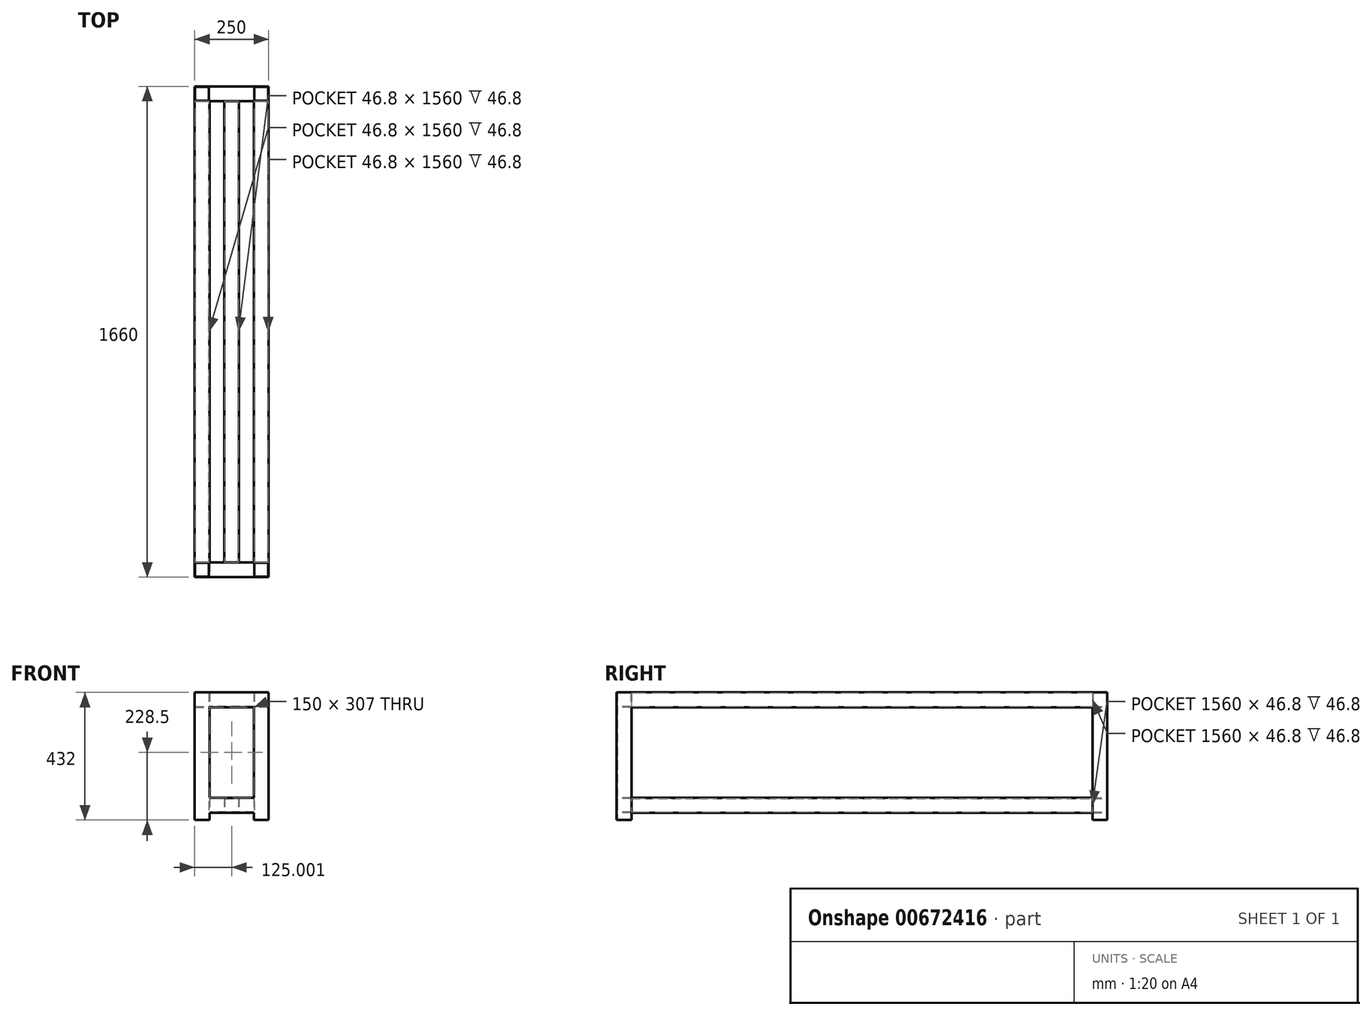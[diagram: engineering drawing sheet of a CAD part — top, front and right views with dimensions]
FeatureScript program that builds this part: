
annotation { "Feature Type Name" : "Feature", "Feature Type Description" : "" }
export const myFeature = defineFeature(function(context is Context, id is Id, definition is map)
    precondition{}
    {
        {
            var Q0;
            Q0=qCreatedBy(makeId("Top.planeOp"),FACE);
            var sketch = newSketch(context, id + "F0", { "sketchPlane" : qUnion([Q0])});
            skLineSegment(sketch, "E0.bottom", {"start": v(-25.56, 22.59) * mm, "end": v(24.44, 22.59) * mm});
            skLineSegment(sketch, "E0.top", {"start": v(-25.56, -27.41) * mm, "end": v(24.44, -27.41) * mm});
            skLineSegment(sketch, "E0.left", {"start": v(-25.56, 22.59) * mm, "end": v(-25.56, -27.41) * mm});
            skLineSegment(sketch, "E0.right", {"start": v(24.44, 22.59) * mm, "end": v(24.44, -27.41) * mm});
            skLineSegment(sketch, "E1.bottom", {"start": v(-23.96, 20.99) * mm, "end": v(22.84, 20.99) * mm});
            skLineSegment(sketch, "E1.top", {"start": v(-23.96, -25.81) * mm, "end": v(22.84, -25.81) * mm});
            skLineSegment(sketch, "E1.left", {"start": v(-23.96, 20.99) * mm, "end": v(-23.96, -25.81) * mm});
            skLineSegment(sketch, "E1.right", {"start": v(22.84, 20.99) * mm, "end": v(22.84, -25.81) * mm});
            skSolve(sketch);
        }
        {
            var Q0;
            Q0 = qSketchRegion(id + "F0", true);
            extrude(context, id + "F1", {"entities" : qUnion([Q0]), "depth" : 432 * mm, "offsetDistance" : 25 * mm});
        }
        {
            var Q0;
            Q0=makeQuery(id+"F1.opExtrude","SWEPT_FACE",FACE,{"disambiguationData":[OSD([sQuery(id+"F0.wireOp",EDGE,"E0.right")])]});
            var sketch = newSketch(context, id + "F2", { "sketchPlane" : qUnion([Q0])});
            skLineSegment(sketch, "E2.bottom", {"start": v(-27.41, 75) * mm, "end": v(22.59, 75) * mm});
            skLineSegment(sketch, "E2.top", {"start": v(-27.41, 25) * mm, "end": v(22.59, 25) * mm});
            skLineSegment(sketch, "E2.left", {"start": v(-27.41, 75) * mm, "end": v(-27.41, 25) * mm});
            skLineSegment(sketch, "E2.right", {"start": v(22.59, 75) * mm, "end": v(22.59, 25) * mm});
            skLineSegment(sketch, "E3.bottom", {"start": v(-25.81, 73.4) * mm, "end": v(20.99, 73.4) * mm});
            skLineSegment(sketch, "E3.top", {"start": v(-25.81, 26.6) * mm, "end": v(20.99, 26.6) * mm});
            skLineSegment(sketch, "E3.left", {"start": v(-25.81, 73.4) * mm, "end": v(-25.81, 26.6) * mm});
            skLineSegment(sketch, "E3.right", {"start": v(20.99, 73.4) * mm, "end": v(20.99, 26.6) * mm});
            skLineSegment(sketch, "E4.bottom", {"start": v(-27.41, 432) * mm, "end": v(22.59, 432) * mm});
            skLineSegment(sketch, "E4.top", {"start": v(-27.41, 382) * mm, "end": v(22.59, 382) * mm});
            skLineSegment(sketch, "E4.left", {"start": v(-27.41, 432) * mm, "end": v(-27.41, 382) * mm});
            skLineSegment(sketch, "E4.right", {"start": v(22.59, 432) * mm, "end": v(22.59, 382) * mm});
            skLineSegment(sketch, "E5.bottom", {"start": v(-25.81, 430.4) * mm, "end": v(20.99, 430.4) * mm});
            skLineSegment(sketch, "E5.top", {"start": v(-25.81, 383.6) * mm, "end": v(20.99, 383.6) * mm});
            skLineSegment(sketch, "E5.left", {"start": v(-25.81, 430.4) * mm, "end": v(-25.81, 383.6) * mm});
            skLineSegment(sketch, "E5.right", {"start": v(20.99, 430.4) * mm, "end": v(20.99, 383.6) * mm});
            skSolve(sketch);
        }
        {
            var Q0;
            Q0 = qSketchRegion(id + "F2", true);
            extrude(context, id + "F3", {"entities" : qUnion([Q0]), "operationType" : NewBodyOperationType.ADD, "depth" : 75 * mm, "offsetDistance" : 25 * mm});
        }
        {
            var Q0;
            Q0=makeQuery(id+"F3.boolean.opBoolean","MERGE",FACE,{"derivedFrom":[makeQuery(id+"F1.opExtrude","SWEPT_FACE",FACE,{"disambiguationData":[OSD([sQuery(id+"F0.wireOp",EDGE,"E0.top")])]}),makeQuery(id+"F3.opExtrude","SWEPT_FACE",FACE,{"disambiguationData":[OSD([sQuery(id+"F2.wireOp",EDGE,"E2.left")])]}),makeQuery(id+"F3.opExtrude","SWEPT_FACE",FACE,{"disambiguationData":[OSD([sQuery(id+"F2.wireOp",EDGE,"E4.left")])]})]});
            var sketch = newSketch(context, id + "F4", { "sketchPlane" : qUnion([Q0])});
            skLineSegment(sketch, "E6.bottom", {"start": v(-25.56, 432) * mm, "end": v(24.44, 432) * mm});
            skLineSegment(sketch, "E6.top", {"start": v(-25.56, 382) * mm, "end": v(24.44, 382) * mm});
            skLineSegment(sketch, "E6.left", {"start": v(-25.56, 432) * mm, "end": v(-25.56, 382) * mm});
            skLineSegment(sketch, "E6.right", {"start": v(24.44, 432) * mm, "end": v(24.44, 382) * mm});
            skLineSegment(sketch, "E7.bottom", {"start": v(-23.96, 430.4) * mm, "end": v(22.84, 430.4) * mm});
            skLineSegment(sketch, "E7.top", {"start": v(-23.96, 383.6) * mm, "end": v(22.84, 383.6) * mm});
            skLineSegment(sketch, "E7.left", {"start": v(-23.96, 430.4) * mm, "end": v(-23.96, 383.6) * mm});
            skLineSegment(sketch, "E7.right", {"start": v(22.84, 430.4) * mm, "end": v(22.84, 383.6) * mm});
            skLineSegment(sketch, "E8.bottom", {"start": v(74.44, 75) * mm, "end": v(99.44, 75) * mm});
            skLineSegment(sketch, "E8.top", {"start": v(74.44, 25) * mm, "end": v(99.44, 25) * mm});
            skLineSegment(sketch, "E8.left", {"start": v(74.44, 75) * mm, "end": v(74.44, 25) * mm});
            skLineSegment(sketch, "E8.right", {"start": v(99.44, 75) * mm, "end": v(99.44, 73.4) * mm});
            skLineSegment(sketch, "E9.bottom", {"start": v(76.04, 73.4) * mm, "end": v(99.44, 73.4) * mm});
            skLineSegment(sketch, "E9.top", {"start": v(76.04, 26.6) * mm, "end": v(99.44, 26.6) * mm});
            skLineSegment(sketch, "E9.left", {"start": v(76.04, 73.4) * mm, "end": v(76.04, 26.6) * mm});
            skLineSegment(sketch, "E10.trimOffspring", {"start": v(99.44, 26.6) * mm, "end": v(99.44, 25) * mm});
            skSolve(sketch);
        }
        {
            var Q0;
            Q0 = qSketchRegion(id + "F4", true);
            extrude(context, id + "F5", {"entities" : qUnion([Q0]), "operationType" : NewBodyOperationType.ADD, "depth" : 780 * mm, "offsetDistance" : 25 * mm});
        }
        {
            var Q0;
            Q0=makeQuery(id+"F1.opExtrude","SWEPT_BODY",BODY,{"disambiguationData":[OSD([sQuery(id+"F0.wireOp",EDGE,"E0.bottom"),sQuery(id+"F0.wireOp",EDGE,"E0.top"),sQuery(id+"F0.wireOp",EDGE,"E0.left"),sQuery(id+"F0.wireOp",EDGE,"E0.right"),sQuery(id+"F0.wireOp",EDGE,"E1.bottom"),sQuery(id+"F0.wireOp",EDGE,"E1.top"),sQuery(id+"F0.wireOp",EDGE,"E1.left"),sQuery(id+"F0.wireOp",EDGE,"E1.right")])]});
            var Q1;
            Q1=makeQuery(id+"F5.opExtrude","CAP_FACE",FACE,{"disambiguationData":[OSD([sQuery(id+"F4.wireOp",EDGE,"E6.bottom"),sQuery(id+"F4.wireOp",EDGE,"E6.top"),sQuery(id+"F4.wireOp",EDGE,"E6.left"),sQuery(id+"F4.wireOp",EDGE,"E6.right"),sQuery(id+"F4.wireOp",EDGE,"E7.bottom"),sQuery(id+"F4.wireOp",EDGE,"E7.top"),sQuery(id+"F4.wireOp",EDGE,"E7.left"),sQuery(id+"F4.wireOp",EDGE,"E7.right")])],"isStart":false});
            mirror(context, id + "F6", {"operationType" : NewBodyOperationType.ADD, "entities" : qUnion([Q0]), "mirrorPlane" : qUnion([Q1])});
        }
        {
            var Q0;
            Q0=makeQuery(id+"F1.opExtrude","SWEPT_BODY",BODY,{"disambiguationData":[OSD([sQuery(id+"F0.wireOp",EDGE,"E0.bottom"),sQuery(id+"F0.wireOp",EDGE,"E0.top"),sQuery(id+"F0.wireOp",EDGE,"E0.left"),sQuery(id+"F0.wireOp",EDGE,"E0.right"),sQuery(id+"F0.wireOp",EDGE,"E1.bottom"),sQuery(id+"F0.wireOp",EDGE,"E1.top"),sQuery(id+"F0.wireOp",EDGE,"E1.left"),sQuery(id+"F0.wireOp",EDGE,"E1.right")])]});
            var Q1;
            Q1=makeQuery(id+"F6.opPattern","COPY",FACE,{"derivedFrom":makeQuery(id+"F3.opExtrude","CAP_FACE",FACE,{"disambiguationData":[OSD([sQuery(id+"F2.wireOp",EDGE,"E4.bottom"),sQuery(id+"F2.wireOp",EDGE,"E4.top"),sQuery(id+"F2.wireOp",EDGE,"E4.left"),sQuery(id+"F2.wireOp",EDGE,"E4.right"),sQuery(id+"F2.wireOp",EDGE,"E5.bottom"),sQuery(id+"F2.wireOp",EDGE,"E5.top"),sQuery(id+"F2.wireOp",EDGE,"E5.left"),sQuery(id+"F2.wireOp",EDGE,"E5.right")])],"isStart":false}),"instanceName":"1"});
            mirror(context, id + "F7", {"operationType" : NewBodyOperationType.ADD, "entities" : qUnion([Q0]), "mirrorPlane" : qUnion([Q1])});
        }
    });
